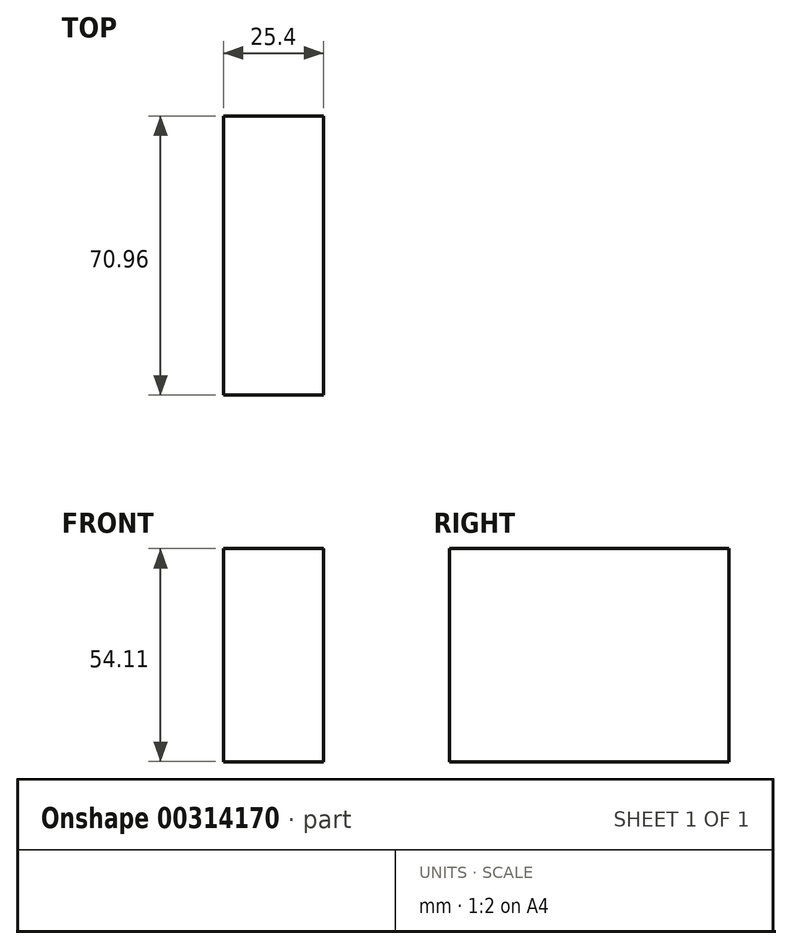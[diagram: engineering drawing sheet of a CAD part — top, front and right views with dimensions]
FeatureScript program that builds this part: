
annotation { "Feature Type Name" : "Feature", "Feature Type Description" : "" }
export const myFeature = defineFeature(function(context is Context, id is Id, definition is map)
    precondition{}
    {
        {
            var Q0;
            Q0=qCreatedBy(makeId("Right.planeOp"),FACE);
            var sketch = newSketch(context, id + "F0", { "sketchPlane" : qUnion([Q0])});
            skLineSegment(sketch, "E0.bottom", {"start": v(0, 0) * mm, "end": v(70.96, 0) * mm});
            skLineSegment(sketch, "E0.top", {"start": v(0, -54.11) * mm, "end": v(70.96, -54.11) * mm});
            skLineSegment(sketch, "E0.left", {"start": v(0, 0) * mm, "end": v(0, -54.11) * mm});
            skLineSegment(sketch, "E0.right", {"start": v(70.96, 0) * mm, "end": v(70.96, -54.11) * mm});
            skSolve(sketch);
        }
        {
            var Q0;
            Q0=makeQuery(id+"F0.imprint","IMPRINT",FACE,{"disambiguationData":[TD([[makeQuery(id+"F0.imprint","IMPRINT",EDGE,{"derivedFrom":sQuery(id+"F0.wireOp",EDGE,"E0.bottom")}),-1.0]])]});
            extrude(context, id + "F1", {"entities" : qUnion([Q0]), "depth" : 25.4 * mm});
        }
    });
